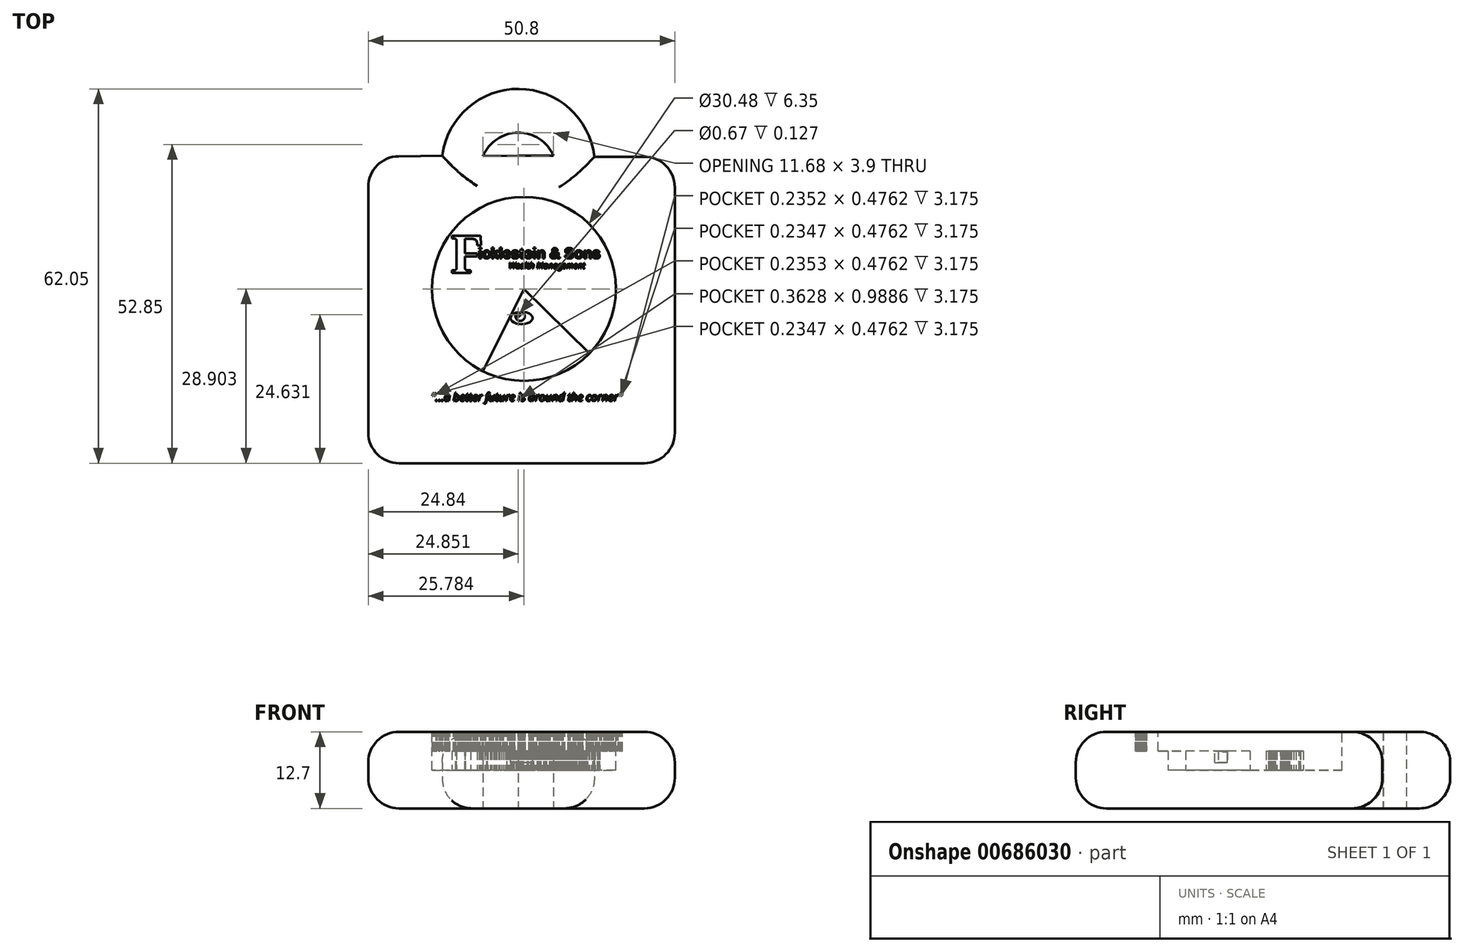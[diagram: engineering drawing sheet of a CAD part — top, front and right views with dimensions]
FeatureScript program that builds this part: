
annotation { "Feature Type Name" : "Feature", "Feature Type Description" : "" }
export const myFeature = defineFeature(function(context is Context, id is Id, definition is map)
    precondition{}
    {
        {
            var Q0;
            Q0=qCreatedBy(makeId("Top.planeOp"),FACE);
            var sketch = newSketch(context, id + "F0", { "sketchPlane" : qUnion([Q0])});
            skLineSegment(sketch, "E0.top", {"start": v(-47.58, -20.5) * mm, "end": v(3.22, -20.5) * mm});
            skLineSegment(sketch, "E0.left", {"start": v(-47.58, 30.3) * mm, "end": v(-47.58, -20.5) * mm});
            skLineSegment(sketch, "E0.right", {"start": v(3.22, 30.3) * mm, "end": v(3.22, -20.5) * mm});
            skArc(sketch, "E1", {"start": v(-10.11, 30.32) * mm, "mid": v(-22.64, 41.55) * mm, "end": v(-35.32, 30.48) * mm});
            skLineSegment(sketch, "E2", {"start": v(-47.58, 30.3) * mm, "end": v(-35.32, 30.48) * mm});
            skLineSegment(sketch, "E3", {"start": v(3.22, 30.3) * mm, "end": v(-10.11, 30.32) * mm});
            skLineSegment(sketch, "E4", {"start": v(-22.73, 30.48) * mm, "end": v(-28.57, 30.4) * mm});
            skLineSegment(sketch, "E5", {"start": v(-22.73, 30.48) * mm, "end": v(-16.89, 30.48) * mm});
            skArc(sketch, "E6", {"start": v(-16.89, 30.48) * mm, "mid": v(-22.76, 34.3) * mm, "end": v(-28.57, 30.4) * mm});
            skSolve(sketch);
        }
        {
            var Q0;
            Q0 = qSketchRegion(id + "F0", true);
            extrude(context, id + "F1", {"entities" : qUnion([Q0]), "depth" : 12.7 * mm, "offsetDistance" : 25.4 * mm});
        }
        {
            var Q0;
            Q0=makeQuery(id+"F1.opExtrude","CAP_EDGE",EDGE,{"disambiguationData":[OSD([sQuery(id+"F0.wireOp",EDGE,"E2")])],"isStart":false});
            var Q1;
            Q1=makeQuery(id+"F1.opExtrude","SWEPT_EDGE",EDGE,{"disambiguationData":[OSD([sQuery(id+"F0.wireOp",EDGE,"E0.left"),sQuery(id+"F0.wireOp",EDGE,"E2")])]});
            var Q2;
            Q2=makeQuery(id+"F1.opExtrude","CAP_EDGE",EDGE,{"disambiguationData":[OSD([sQuery(id+"F0.wireOp",EDGE,"E0.left")])],"isStart":false});
            var Q3;
            Q3=makeQuery(id+"F1.opExtrude","CAP_EDGE",EDGE,{"disambiguationData":[OSD([sQuery(id+"F0.wireOp",EDGE,"E0.left")])],"isStart":true});
            var Q4;
            Q4=makeQuery(id+"F1.opExtrude","CAP_EDGE",EDGE,{"disambiguationData":[OSD([sQuery(id+"F0.wireOp",EDGE,"E2")])],"isStart":true});
            var Q5;
            Q5=makeQuery(id+"F1.opExtrude","SWEPT_EDGE",EDGE,{"disambiguationData":[OSD([sQuery(id+"F0.wireOp",EDGE,"E0.top"),sQuery(id+"F0.wireOp",EDGE,"E0.left")])]});
            var Q6;
            Q6=makeQuery(id+"F1.opExtrude","CAP_EDGE",EDGE,{"disambiguationData":[OSD([sQuery(id+"F0.wireOp",EDGE,"E0.top")])],"isStart":true});
            var Q7;
            Q7=makeQuery(id+"F1.opExtrude","CAP_EDGE",EDGE,{"disambiguationData":[OSD([sQuery(id+"F0.wireOp",EDGE,"E0.top")])],"isStart":false});
            var Q8;
            Q8=makeQuery(id+"F1.opExtrude","CAP_EDGE",EDGE,{"disambiguationData":[OSD([sQuery(id+"F0.wireOp",EDGE,"E0.right")])],"isStart":false});
            var Q9;
            Q9=makeQuery(id+"F1.opExtrude","CAP_EDGE",EDGE,{"disambiguationData":[OSD([sQuery(id+"F0.wireOp",EDGE,"E0.right")])],"isStart":true});
            var Q10;
            Q10=makeQuery(id+"F1.opExtrude","SWEPT_EDGE",EDGE,{"disambiguationData":[OSD([sQuery(id+"F0.wireOp",EDGE,"E0.top"),sQuery(id+"F0.wireOp",EDGE,"E0.right")])]});
            var Q11;
            Q11=makeQuery(id+"F1.opExtrude","CAP_EDGE",EDGE,{"disambiguationData":[OSD([sQuery(id+"F0.wireOp",EDGE,"E3")])],"isStart":false});
            var Q12;
            Q12=makeQuery(id+"F1.opExtrude","CAP_EDGE",EDGE,{"disambiguationData":[OSD([sQuery(id+"F0.wireOp",EDGE,"E3")])],"isStart":true});
            var Q13;
            Q13=makeQuery(id+"F1.opExtrude","SWEPT_EDGE",EDGE,{"disambiguationData":[OSD([sQuery(id+"F0.wireOp",EDGE,"E0.right"),sQuery(id+"F0.wireOp",EDGE,"E3")])]});
            var Q14;
            Q14=makeQuery(id+"F1.opExtrude","CAP_EDGE",EDGE,{"disambiguationData":[OSD([sQuery(id+"F0.wireOp",EDGE,"E1")])],"isStart":false});
            var Q15;
            Q15=makeQuery(id+"F1.opExtrude","CAP_EDGE",EDGE,{"disambiguationData":[OSD([sQuery(id+"F0.wireOp",EDGE,"E1")])],"isStart":true});
            fillet(context, id + "F2", {"entities" : qUnion([Q0, Q1, Q2, Q3, Q4, Q5, Q6, Q7, Q8, Q9, Q10, Q11, Q12, Q13, Q14, Q15]), "radius" : 5.08 * mm, "tangentPropagation" : true, "allowEdgeOverflow" : false});
        }
        {
            var Q0;
            Q0=makeQuery(id+"F1.opExtrude","CAP_FACE",FACE,{"disambiguationData":[OSD([sQuery(id+"F0.wireOp",EDGE,"E0.top"),sQuery(id+"F0.wireOp",EDGE,"E0.left"),sQuery(id+"F0.wireOp",EDGE,"E0.right"),sQuery(id+"F0.wireOp",EDGE,"E1"),sQuery(id+"F0.wireOp",EDGE,"E2"),sQuery(id+"F0.wireOp",EDGE,"E3"),sQuery(id+"F0.wireOp",EDGE,"E4"),sQuery(id+"F0.wireOp",EDGE,"E5"),sQuery(id+"F0.wireOp",EDGE,"E6")])],"isStart":false});
            var sketch = newSketch(context, id + "F3", { "sketchPlane" : qUnion([Q0])});
            skCircle(sketch, "E7", {"center": v(-21.8, 8.4) * mm, "radius": 15.24 * mm});
            skSolve(sketch);
        }
        {
            var Q0;
            Q0 = qSketchRegion(id + "F3", true);
            extrude(context, id + "F4", {"entities" : qUnion([Q0]), "operationType" : NewBodyOperationType.REMOVE, "oppositeDirection" : true, "depth" : 6.35 * mm, "offsetDistance" : 25.4 * mm});
        }
        {
            var Q0;
            Q0=makeQuery(id+"F3.imprint","IMPRINT",FACE,{"disambiguationData":[TD([[makeQuery(id+"F3.imprint","IMPRINT",EDGE,{"derivedFrom":sQuery(id+"F3.wireOp",EDGE,"E7")}),1.0]])]});
            var sketch = newSketch(context, id + "F5", { "sketchPlane" : qUnion([Q0])});
            skEllipse(sketch, "E8", {"center": v(-22.57, 2.07) * mm, "majorRadius": 2.26 * mm, "minorRadius": 1.3 * mm, "majorAxis": v(1, 0)});
            skCircle(sketch, "E9", {"center": v(-22.79, 2.42) * mm, "radius": 0.92 * mm});
            skSolve(sketch);
        }
        {
            var Q0;
            Q0=makeQuery(id+"F4.boolean.opBoolean","COPY",FACE,{"derivedFrom":makeQuery(id+"F4.opExtrude","CAP_FACE",FACE,{"disambiguationData":[OSD([sQuery(id+"F3.wireOp",EDGE,"E7")])],"isStart":false})});
            var sketch = newSketch(context, id + "F6", { "sketchPlane" : qUnion([Q0])});
            skLineSegment(sketch, "E10", {"start": v(-21.8, 8.4) * mm, "end": v(-28.6, -5.23) * mm});
            skLineSegment(sketch, "E11", {"start": v(-21.8, 8.4) * mm, "end": v(-16.67, -5.95) * mm});
            skLineSegment(sketch, "E12", {"start": v(-21.8, 8.4) * mm, "end": v(-10.95, -2.3) * mm});
            skArc(sketch, "E13", {"start": v(-28.6, -5.23) * mm, "mid": v(-22.71, -6.83) * mm, "end": v(-16.67, -5.95) * mm});
            skArc(sketch, "E14", {"start": v(-16.67, -5.95) * mm, "mid": v(-13.56, -4.51) * mm, "end": v(-10.95, -2.3) * mm});
            skText(sketch, "E15", { "text": "icklestein & Sons", "fontName": "Arimo-Bold.ttf"});
            skText(sketch, "E16", { "text": "F", "fontName": "NotoSerif-Bold.ttf"});
            skText(sketch, "E17", { "text": "Wealth Management ", "fontName": "OpenSans-Italic.ttf"});
            const initialGuessF6  = {"E15": [-0.02936, 0.01347, 1, 0, 0.00176], "E16": [-0.03399, 0.01102, 1, 0, 0.00623], "E17": [-0.02432, 0.01179, 1, 0, 0.001]};
            skSetInitialGuess(sketch, initialGuessF6);
            skSolve(sketch);
        }
        {
            var Q0;
            Q0 = qSketchRegion(id + "F6", true);
            extrude(context, id + "F7", {"entities" : qUnion([Q0]), "operationType" : NewBodyOperationType.ADD, "depth" : 3.17 * mm, "offsetDistance" : 25.4 * mm});
        }
        {
            var Q0;
            Q0=makeQuery(id+"F1.opExtrude","CAP_FACE",FACE,{"disambiguationData":[OSD([sQuery(id+"F0.wireOp",EDGE,"E0.top"),sQuery(id+"F0.wireOp",EDGE,"E0.left"),sQuery(id+"F0.wireOp",EDGE,"E0.right"),sQuery(id+"F0.wireOp",EDGE,"E1"),sQuery(id+"F0.wireOp",EDGE,"E2"),sQuery(id+"F0.wireOp",EDGE,"E3"),sQuery(id+"F0.wireOp",EDGE,"E4"),sQuery(id+"F0.wireOp",EDGE,"E5"),sQuery(id+"F0.wireOp",EDGE,"E6")])],"isStart":false});
            var sketch = newSketch(context, id + "F8", { "sketchPlane" : qUnion([Q0])});
            skText(sketch, "E18", { "text": "\"...a better future is around the corner\"", "fontName": "OpenSans-Italic.ttf"});
            const initialGuessF8  = {"E18": [-0.03716, -0.01018, 1, 0, 0.00133]};
            skSetInitialGuess(sketch, initialGuessF8);
            skSolve(sketch);
        }
        {
            var Q0;
            Q0 = qSketchRegion(id + "F8", true);
            extrude(context, id + "F9", {"entities" : qUnion([Q0]), "operationType" : NewBodyOperationType.REMOVE, "oppositeDirection" : true, "depth" : 3.17 * mm, "offsetDistance" : 25.4 * mm});
        }
        {
            var Q0;
            Q0=sQuery(id+"F6.wireOp",EDGE,"E11");
            extrude(context, id + "F10", {"bodyType" : ToolBodyType.SURFACE, "surfaceEntities" : qUnion([Q0]), "depth" : 3.17 * mm, "offsetDistance" : 25.4 * mm});
        }
        {
            var Q0;
            Q0=makeQuery(id+"F7.opExtrude","CAP_FACE",FACE,{"disambiguationData":[OSD([sQuery(id+"F6.wireOp",EDGE,"E10"),sQuery(id+"F6.wireOp",EDGE,"E12"),sQuery(id+"F6.wireOp",EDGE,"E13"),sQuery(id+"F6.wireOp",EDGE,"E14")])],"isStart":false});
            var sketch = newSketch(context, id + "F11", { "sketchPlane" : qUnion([Q0])});
            skEllipse(sketch, "E19", {"center": v(-22.19, 3.58) * mm, "majorRadius": 1.83 * mm, "minorRadius": 1.03 * mm, "majorAxis": v(1, 0)});
            skSolve(sketch);
        }
        {
            var Q0;
            Q0=makeQuery(id+"F11.imprint","IMPRINT",FACE,{"disambiguationData":[TD([[makeQuery(id+"F11.imprint","IMPRINT",EDGE,{"derivedFrom":sQuery(id+"F11.wireOp",EDGE,"E19")}),1.0]])]});
            var Q1;
            Q1=sQuery(id+"F11.wireOp",EDGE,"E19");
            extrude(context, id + "F12", {"entities" : qUnion([Q0]), "operationType" : NewBodyOperationType.REMOVE, "surfaceEntities" : qUnion([Q1]), "oppositeDirection" : true, "depth" : 1.9 * mm, "offsetDistance" : 25.4 * mm});
        }
        {
            var Q0;
            Q0=makeQuery(id+"F12.boolean.opBoolean","COPY",FACE,{"derivedFrom":makeQuery(id+"F12.opExtrude","CAP_FACE",FACE,{"disambiguationData":[OSD([sQuery(id+"F11.wireOp",EDGE,"E19")])],"isStart":false})});
            var sketch = newSketch(context, id + "F13", { "sketchPlane" : qUnion([Q0])});
            skCircle(sketch, "E20", {"center": v(-22.4, 3.86) * mm, "radius": 0.77 * mm});
            skSolve(sketch);
        }
        {
            var Q0;
            {var subQ0=sQuery(id+"F13.wireOp",EDGE,"E20");var subQ1=makeQuery(id+"F12.boolean.opBoolean","COPY",EDGE,{"derivedFrom":makeQuery(id+"F12.opExtrude","CAP_EDGE",EDGE,{"disambiguationData":[OSD([sQuery(id+"F11.wireOp",EDGE,"E19")])],"isStart":false})});var subQ2=makeQuery(id+"F13.imprint","INTERSECT",VERTEX,{"disambiguationData":[OD(0.0)],"derivedFrom":[subQ1,subQ0]});Q0=makeQuery(id+"F13.imprint","IMPRINT",FACE,{"disambiguationData":[TD([[makeQuery(id+"F13.imprint","IMPRINT",EDGE,{"disambiguationData":[TD([[subQ2,-1.0]])],"derivedFrom":subQ0}),1.0]])]});}
            var Q1;
            Q1=sQuery(id+"F13.wireOp",EDGE,"E20");
            extrude(context, id + "F14", {"entities" : qUnion([Q0]), "operationType" : NewBodyOperationType.ADD, "surfaceEntities" : qUnion([Q1]), "depth" : 1.9 * mm, "offsetDistance" : 25.4 * mm});
        }
        {
            var Q0;
            Q0=makeQuery(id+"F14.boolean.opBoolean","MERGE",FACE,{"derivedFrom":[makeQuery(id+"F7.opExtrude","CAP_FACE",FACE,{"disambiguationData":[OSD([sQuery(id+"F6.wireOp",EDGE,"E10"),sQuery(id+"F6.wireOp",EDGE,"E12"),sQuery(id+"F6.wireOp",EDGE,"E13"),sQuery(id+"F6.wireOp",EDGE,"E14")])],"isStart":false}),makeQuery(id+"F14.opExtrude","CAP_FACE",FACE,{"disambiguationData":[OSD([sQuery(id+"F11.wireOp",EDGE,"E19"),sQuery(id+"F13.wireOp",EDGE,"E20")])],"isStart":false})]});
            var sketch = newSketch(context, id + "F15", { "sketchPlane" : qUnion([Q0])});
            skCircle(sketch, "E21", {"center": v(-22.74, 4.13) * mm, "radius": 0.34 * mm});
            skSolve(sketch);
        }
        {
            var Q0;
            Q0=makeQuery(id+"F15.imprint","IMPRINT",FACE,{"disambiguationData":[TD([[makeQuery(id+"F15.imprint","IMPRINT",EDGE,{"derivedFrom":sQuery(id+"F15.wireOp",EDGE,"E21")}),1.0]])]});
            extrude(context, id + "F16", {"entities" : qUnion([Q0]), "operationType" : NewBodyOperationType.REMOVE, "oppositeDirection" : true, "depth" : 0.13 * mm, "offsetDistance" : 25.4 * mm});
        }
    });
